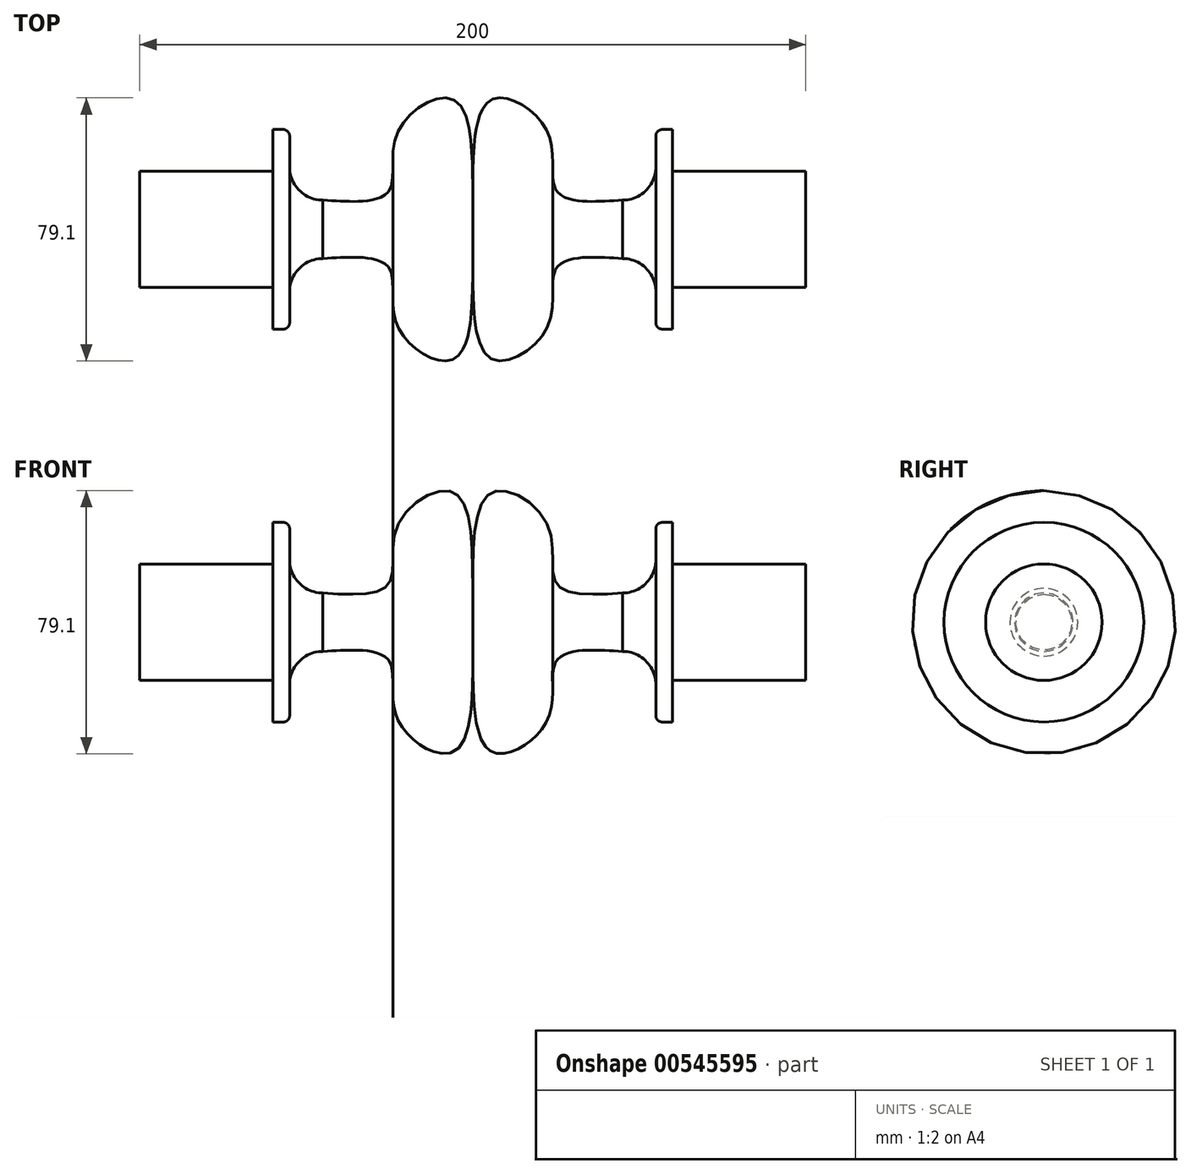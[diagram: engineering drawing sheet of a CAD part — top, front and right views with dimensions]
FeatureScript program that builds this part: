
annotation { "Feature Type Name" : "Feature", "Feature Type Description" : "" }
export const myFeature = defineFeature(function(context is Context, id is Id, definition is map)
    precondition{}
    {
        {
            var Q0;
            Q0=qCreatedBy(makeId("Front.planeOp"),FACE);
            var sketch = newSketch(context, id + "F0", { "sketchPlane" : qUnion([Q0])});
            skLineSegment(sketch, "E0", {"start": v(0, 0) * mm, "end": v(100, 0) * mm});
            skLineSegment(sketch, "E1", {"start": v(100, 0) * mm, "end": v(100, 17.5) * mm});
            skLineSegment(sketch, "E2", {"start": v(100, 17.5) * mm, "end": v(60, 17.5) * mm});
            skLineSegment(sketch, "E3", {"start": v(60, 17.5) * mm, "end": v(60, 30) * mm});
            skLineSegment(sketch, "E4", {"start": v(60, 30) * mm, "end": v(56.9, 30) * mm});
            skLineSegment(sketch, "E5", {"start": v(55, 28.1) * mm, "end": v(55, 18.77) * mm});
            skLineSegment(sketch, "E6", {"start": v(0, 0) * mm, "end": v(0, 8.77) * mm});
            skPoint(sketch, "E7.start.orphan", {"position": v(-54.63, 17.5) * mm});
            skPoint(sketch, "E8.start.orphan", {"position": v(-31.62, 30) * mm});
            skPoint(sketch, "E9.start.orphan", {"position": v(-26.62, 19.77) * mm});
            skPoint(sketch, "E10.orphan", {"position": v(-26.62, 8.77) * mm});
            skPoint(sketch, "E11.orphan", {"position": v(-54.63, 0) * mm});
            skPoint(sketch, "E12.visualSharp", {"position": v(55, 8.77) * mm});
            skArc(sketch, "E12.filletArc", {"start": v(45, 8.77) * mm, "mid": v(52.07, 11.7) * mm, "end": v(55, 18.77) * mm});
            skPoint(sketch, "E13.visualSharp", {"position": v(55, 30) * mm});
            skArc(sketch, "E13.filletArc", {"start": v(56.9, 30) * mm, "mid": v(55.55, 29.45) * mm, "end": v(55, 28.1) * mm});
            skFitSpline(sketch, "E14", {"points": [v(0, 8.77) * mm, v(6.17, 39.18) * mm, v(22.66, 28.92) * mm, v(25.23, 11.52) * mm, v(45, 8.77) * mm], "startDerivative": vector(-0.02, 140.82) * mm, "endDerivative": vector(106.97, 6.81) * mm});
            skSolve(sketch);
        }
        {
            var Q0;
            Q0=makeQuery(id+"F0.imprint","IMPRINT",FACE,{"disambiguationData":[TD([[makeQuery(id+"F0.imprint","IMPRINT",EDGE,{"derivedFrom":sQuery(id+"F0.wireOp",EDGE,"E0")}),1.0]])]});
            var Q1;
            Q1=sQuery(id+"F0.wireOp",EDGE,"E0");
            revolve(context, id + "F1", {"entities" : qUnion([Q0]), "axis" : qUnion([Q1]), "revolveType" : RevolveType.FULL});
        }
        {
            var Q0;
            Q0=makeQuery(id+"F1.opRevolve","SWEPT_BODY",BODY,{"disambiguationData":[OSD([sQuery(id+"F0.wireOp",EDGE,"E0"),sQuery(id+"F0.wireOp",EDGE,"E1"),sQuery(id+"F0.wireOp",EDGE,"E2"),sQuery(id+"F0.wireOp",EDGE,"E3"),sQuery(id+"F0.wireOp",EDGE,"E4"),sQuery(id+"F0.wireOp",EDGE,"E5"),sQuery(id+"F0.wireOp",EDGE,"UXudH1RW-BmIw-oPte-rXwD-AiGzmQncnfJS"),sQuery(id+"F0.wireOp",EDGE,"E6")])]});
            var Q1;
            Q1=makeQuery(id+"F1.opRevolve","SWEPT_FACE",FACE,{"disambiguationData":[OSD([sQuery(id+"F0.wireOp",EDGE,"E6")])]});
            mirror(context, id + "F2", {"operationType" : NewBodyOperationType.ADD, "entities" : qUnion([Q0]), "mirrorPlane" : qUnion([Q1])});
        }
    });
